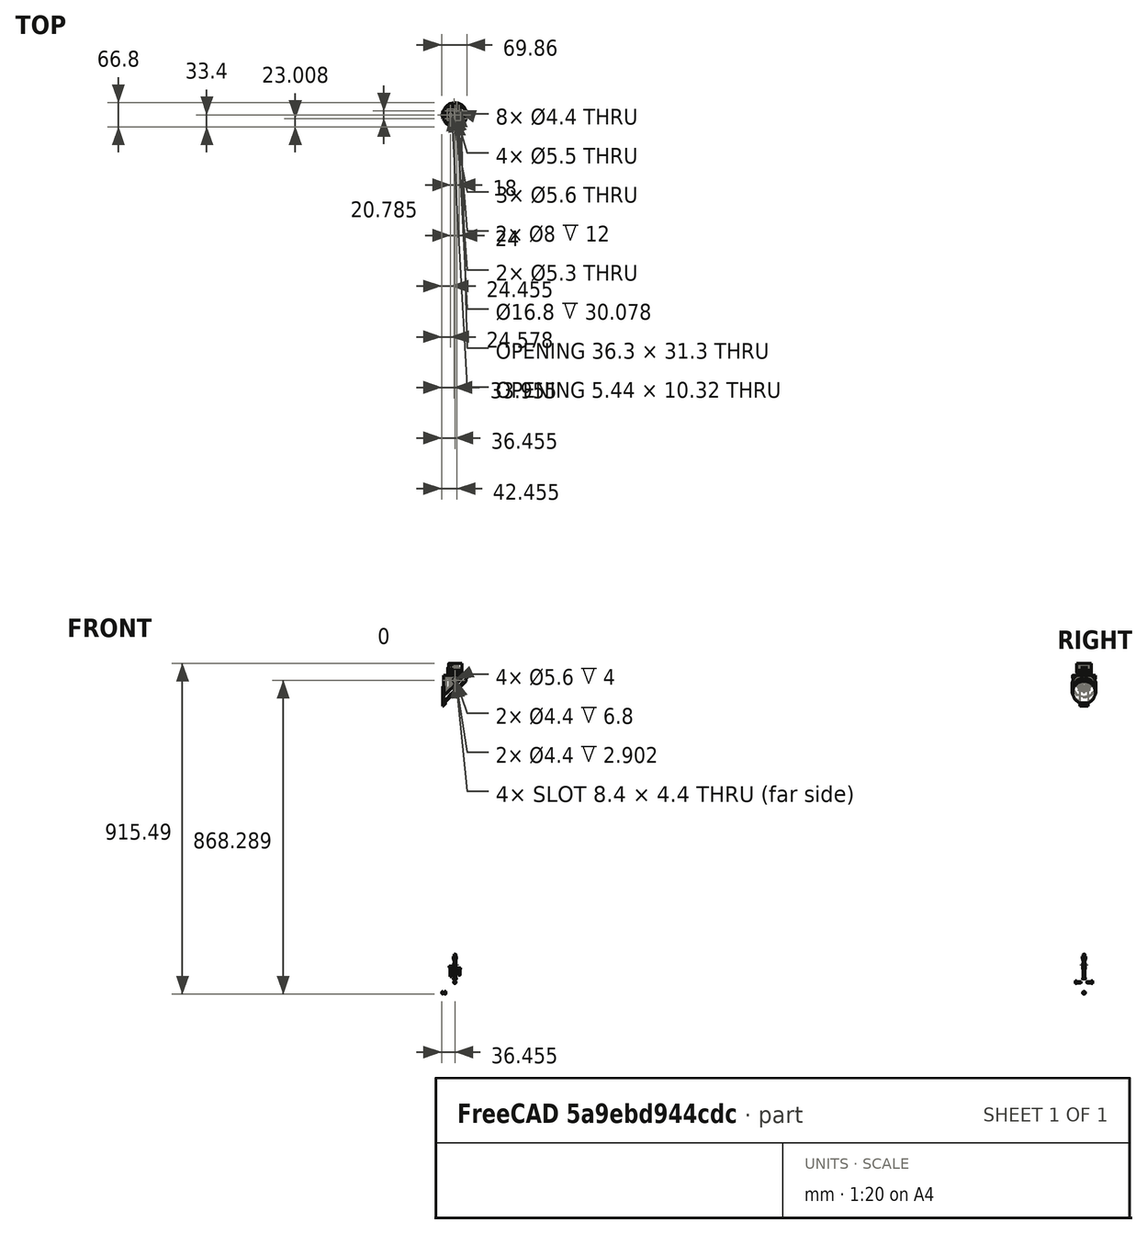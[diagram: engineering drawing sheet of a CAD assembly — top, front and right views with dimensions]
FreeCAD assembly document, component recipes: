
FREECAD ASSEMBLY — COMPONENT RECIPES ("SecondaryMirrorCell")

This assembly document has 9 components, labeled P0..P8 below (a component is one placed body or linked part). 9 of them carry a construction recipe — the FreeCAD feature program that regenerates the part from scratch, quoted from this document or its linked companion documents; the rest are supplied as boundary geometry only. No exploded tour is included for this assembly.
NOTE — document 2 of 2 of this assembly tour. The two overview renders and the header above are repeated from document 1; the component sections below continue where the previous document stopped.
COMPONENT P7 — recipe-attached ("SpiderHub_PushPull", modeled in this document).
Construction recipe (the document's own serialized feature program — sketch geometry with constraints, then the solid features built on it; lengths are millimeters unless a unit is written):

FEATURE [PartDesign::Plane] DatumPlane040  label="SpiderHub_PushPull_DatumPlane_Top"
  AttachmentOffset = pos=(0,0,20) rot=(0,0,1;0rad)
  Length = 60
  MapMode = 5
  Placement = pos=(0,0,20) rot=(0,0,1;0rad)
  ResizeMode = 0
  Support = -> [XY_Plane105]
  Width = 60
  expr: .AttachmentOffset.Base.z = <<Common>>#<<Parameters>>.sec_stalkheight
FEATURE [PartDesign::CoordinateSystem] Local_CS242  label="LCS_SpiderHub_PushPull_Lower"
  AttacherType = Attacher::AttachEngine3D
  AttachmentOffset = pos=(0,0,0) rot=(0,0,1;1.5708rad)
  MapMode = 5
  Placement = pos=(0,0,0) rot=(0,0,1;1.5708rad)
  Support = -> [XY_Plane105]
FEATURE [PartDesign::CoordinateSystem] Local_CS241  label="LCS_SpiderHub_PushPull_BoltTilt"
  AttacherType = Attacher::AttachEngine3D
  AttachmentOffset = pos=(-12,0,8) rot=(0,0,1;0rad)
  MapMode = 5
  Placement = pos=(-12,0,8) rot=(0,0,1;0rad)
  Support = -> [XY_Plane105]
  expr: .AttachmentOffset.Base.x = -<<Common>>#<<Parameters>>.sec_cpointpos
  expr: .AttachmentOffset.Base.z = <<Common>>#<<Parameters>>.sec_pthick
FEATURE [PartDesign::CoordinateSystem] Local_CS240  label="LCS_SpiderHub_PushPull_BoltZrot"
  AttacherType = Attacher::AttachEngine3D
  AttachmentOffset = pos=(12,0,8) rot=(0,0,1;0rad)
  MapMode = 5
  Placement = pos=(12,0,8) rot=(0,0,1;0rad)
  Support = -> [XY_Plane105]
  expr: .AttachmentOffset.Base.x = <<Common>>#<<Parameters>>.sec_cpointpos
  expr: .AttachmentOffset.Base.z = <<Common>>#<<Parameters>>.sec_pthick
FEATURE [PartDesign::CoordinateSystem] Local_CS239  label="LCS_SpiderHub_PushPull_Upper"
  AttacherType = Attacher::AttachEngine3D
  AttachmentOffset = pos=(0,0,20) rot=(0,0,1;1.5708rad)
  MapMode = 5
  Placement = pos=(0,0,20) rot=(0,0,1;1.5708rad)
  Support = -> [XY_Plane105]
  expr: .AttachmentOffset.Base.z = <<Common>>#<<Parameters>>.sec_stalkheight
FEATURE [PartDesign::ShapeBinder] ShapeBinder007  label="SpiderHub_PushPull_ShapeBinder"
  Support = -> [Binder]
  TraceSupport = false
FEATURE [Sketcher::SketchObject] Sketch168  label="SpiderHub_PushPull_Main_Sketch"
  ExternalGeometry = -> [ShapeBinder007]
  FullyConstrained = true
  MapMode = 5
  Support = -> [XY_Plane105]
  expr: Constraints[0] = <<Common>>#<<Parameters>>.sec_centralbolt * 1.1
  expr: Constraints[20] = <<Common>>#<<Parameters>>.sec_fillet
  expr: Constraints[23] = <<Common>>#<<Parameters>>.sec_cpointpos
  expr: Constraints[36] = <<Common>>#<<Parameters>>.sec_collbolt * 1.1
  sketch-geometry (16):
    g0: Circle CenterX=0 CenterY=0 CenterZ=0 NormalX=0 NormalY=0 NormalZ=1 AngleXU=0 Radius=2.75
    g1: LineSegment StartX=-19.1267 StartY=4.61831 StartZ=0 EndX=-4.61831 EndY=19.1267 EndZ=0
    g2: LineSegment StartX=-19.1267 StartY=-4.61831 StartZ=0 EndX=-4.61831 EndY=-19.1267 EndZ=0
    g3: ArcOfCircle CenterX=0 CenterY=0 CenterZ=0 NormalX=0 NormalY=0 NormalZ=1 AngleXU=0 Radius=20 StartAngle=4.53343 EndAngle=8.03294
    g4: ArcOfCircle CenterX=-3.2041 CenterY=17.7125 CenterZ=0 NormalX=0 NormalY=0 NormalZ=1 AngleXU=0 Radius=2 StartAngle=1.74976 EndAngle=2.35619
    g5: ArcOfCircle CenterX=-3.2041 CenterY=-17.7125 CenterZ=0 NormalX=0 NormalY=0 NormalZ=1 AngleXU=0 Radius=2 StartAngle=3.92699 EndAngle=4.53343
    g6: ArcOfCircle CenterX=0 CenterY=0 CenterZ=0 NormalX=0 NormalY=0 NormalZ=1 AngleXU=0 Radius=20 StartAngle=2.96263 EndAngle=3.32055
    g7: ArcOfCircle CenterX=-17.7125 CenterY=-3.2041 CenterZ=0 NormalX=0 NormalY=0 NormalZ=1 AngleXU=0 Radius=2 StartAngle=3.32055 EndAngle=3.92699
    g8: ArcOfCircle CenterX=-17.7125 CenterY=3.2041 CenterZ=0 NormalX=0 NormalY=0 NormalZ=1 AngleXU=0 Radius=2 StartAngle=2.35619 EndAngle=2.96263
    g9: Circle CenterX=0 CenterY=0 CenterZ=0 NormalX=0 NormalY=0 NormalZ=1 AngleXU=0 Radius=12
    g10: LineSegment StartX=-12 StartY=0 StartZ=0 EndX=6 EndY=-10.3923 EndZ=0
    g11: LineSegment StartX=6 StartY=-10.3923 StartZ=0 EndX=6 EndY=10.3923 EndZ=0
    g12: LineSegment StartX=6 StartY=10.3923 StartZ=0 EndX=-12 EndY=0 EndZ=0
    g13: Circle CenterX=-12 CenterY=0 CenterZ=0 NormalX=0 NormalY=0 NormalZ=1 AngleXU=0 Radius=2.2
    g14: Circle CenterX=6 CenterY=10.3923 CenterZ=0 NormalX=0 NormalY=0 NormalZ=1 AngleXU=0 Radius=2.2
    g15: Circle CenterX=6 CenterY=-10.3923 CenterZ=0 NormalX=0 NormalY=0 NormalZ=1 AngleXU=0 Radius=2.2
  constraints (39):
    c: Diameter(g0) = 5.5
    c: Equal(g1,g2)
    c: PointOnObject(g1,g-5)
    c: PointOnObject(g2,g-4)
    c: Coincident(g3,g0)
    c: Coincident(g0,g-3)
    c: Equal(g3,g-3)
    c: Tangent(g1,g4) = 1.5708
    c: Tangent(g2,g5) = -1.5708
    c: Tangent(g3,g5) = -1.5708
    c: Parallel(g2,g-4)
    c: Parallel(g1,g-5)
    c: Equal(g4,g5)
    c: Tangent(g3,g4) = -1.5708
    c: Coincident(g6,g0)
    c: PointOnObject(g6,g-3)
    c: Tangent(g8,g1) = 1.5708
    c: Tangent(g8,g6) = -1.5708
    c: Tangent(g7,g6) = -1.5708
    c: Tangent(g7,g2) = -1.5708
    c: Radius(g8) = 2
    c: Equal(g4,g8)
    c: Coincident(g9,g0)
    c: Radius(g9) = 12
    c: Coincident(g10,g11)
    c: Coincident(g11,g12)
    c: Coincident(g12,g10)
    c: Equal(g10,g11)
    c: Equal(g10,g12)
    c: PointOnObject(g12,g-1)
    c: PointOnObject(g10,g9)
    c: PointOnObject(g10,g9)
    c: PointOnObject(g11,g9)
    c: Coincident(g13,g10)
    c: Coincident(g14,g11)
    c: Coincident(g15,g10)
    c: Diameter(g15) = 4.4
    c: Equal(g15,g14)
    c: Equal(g15,g13)
FEATURE [Sketcher::SketchObject] Sketch169  label="SpiderHub_PushPull_CounterBore_Sketch"
  ExternalGeometry = -> [ShapeBinder007]
  FullyConstrained = true
  MapMode = 5
  Placement = pos=(0,0,20) rot=(0,0,1;0rad)
  Support = -> [DatumPlane040]
  expr: Constraints[0] = <<Common>>#<<Parameters>>.sec_cpointpos
  expr: Constraints[24] = <<Common>>#<<Parameters>>.sec_fillet
  expr: Constraints[3] = <<Common>>#<<Parameters>>.sec_collbolt
  sketch-geometry (18):
    g0: Circle CenterX=0 CenterY=0 CenterZ=0 NormalX=0 NormalY=0 NormalZ=1 AngleXU=0 Radius=12
    g1: ArcOfCircle CenterX=-12 CenterY=0 CenterZ=0 NormalX=0 NormalY=0 NormalZ=1 AngleXU=0 Radius=4 StartAngle=4.71239 EndAngle=7.85398
    g2: LineSegment StartX=-12 StartY=4 StartZ=0 EndX=-14.9166 EndY=4 EndZ=0
    g3: LineSegment StartX=-12 StartY=-4 StartZ=0 EndX=-14.9166 EndY=-4 EndZ=0
    g4: LineSegment StartX=-21 StartY=7.41423 StartZ=0 EndX=-21 EndY=-7.41423 EndZ=0
    g5: ArcOfCircle CenterX=-14.9166 CenterY=6 CenterZ=0 NormalX=0 NormalY=0 NormalZ=1 AngleXU=0 Radius=2 StartAngle=2.35619 EndAngle=4.71239
    g6: GeomPoint X=21 Y=0 Z=0
    g7: GeomPoint X=20 Y=0 Z=0
    g8: GeomPoint X=-20 Y=0 Z=0
    g9: GeomPoint X=-21 Y=0 Z=0
    g10: LineSegment StartX=-16.3308 StartY=7.41423 StartZ=0 EndX=-21 EndY=7.41423 EndZ=0
    g11: LineSegment StartX=-16.3308 StartY=-7.41423 StartZ=0 EndX=-21 EndY=-7.41423 EndZ=0
    g12: ArcOfCircle CenterX=-14.9166 CenterY=-6 CenterZ=0 NormalX=0 NormalY=0 NormalZ=1 AngleXU=0 Radius=2 StartAngle=1.5708 EndAngle=3.927
    g13: LineSegment StartX=-12 StartY=0 StartZ=0 EndX=6 EndY=10.3923 EndZ=0
    g14: LineSegment StartX=6 StartY=10.3923 StartZ=0 EndX=6 EndY=-10.3923 EndZ=0
    g15: LineSegment StartX=6 StartY=-10.3923 StartZ=0 EndX=-12 EndY=0 EndZ=0
    g16: Circle CenterX=6 CenterY=10.3923 CenterZ=0 NormalX=0 NormalY=0 NormalZ=1 AngleXU=0 Radius=4
    g17: Circle CenterX=6 CenterY=-10.3923 CenterZ=0 NormalX=0 NormalY=0 NormalZ=1 AngleXU=0 Radius=4
  constraints (46):
    c: Radius(g0) = 12
    c: Coincident(g0,g-1)
    c: PointOnObject(g1,g0)
    c: Radius(g1) = 4
    c: Horizontal(g2)
    c: Horizontal(g3)
    c: Vertical(g4)
    c: PointOnObject(g7,g-3)
    c: PointOnObject(g8,g-3)
    c: PointOnObject(g9,g4)
    c: PointOnObject(g9,g-1)
    c: PointOnObject(g8,g-1)
    c: DistanceX(g9,g8) = 1
    c: PointOnObject(g7,g-1)
    c: PointOnObject(g6,g-1)
    c: DistanceX(g7,g6) = 1
    c: PointOnObject(g11,g-5)
    c: PointOnObject(g5,g-4)
    c: Coincident(g10,g5)
    c: Coincident(g10,g4)
    c: Coincident(g11,g4)
    c: Horizontal(g11)
    c: Horizontal(g10)
    c: Tangent(g5,g-4)
    c: Radius(g5) = 2
    c: Tangent(g5,g2) = 1.5708
    c: Coincident(g12,g11)
    c: Tangent(g12,g-5)
    c: Tangent(g12,g3) = -1.5708
    c: Equal(g12,g5)
    c: PointOnObject(g13,g-1)
    c: PointOnObject(g13,g0)
    c: Coincident(g14,g13)
    c: PointOnObject(g14,g0)
    c: Coincident(g15,g14)
    c: Coincident(g15,g13)
    c: Equal(g13,g14)
    c: Equal(g14,g15)
    c: Coincident(g1,g3)
    c: Coincident(g1,g13)
    c: Equal(g2,g3)
    c: Coincident(g16,g13)
    c: Coincident(g17,g14)
    c: Equal(g17,g16)
    c: Equal(g16,g1)
    c: Tangent(g2,g1) = -1.5708
FEATURE [PartDesign::Plane] DatumPlane041  label="SpiderHub_PushPull_DatumPlane_SpiderHole"
  Length = 82.6027
  MapMode = 14
  Placement = pos=(-11.8725,-11.8725,0) rot=(0.862856,-0.357407,-0.357407;1.71777rad)
  ResizeMode = 0
  Support = -> [ShapeBinder007,Z_Axis087]
  Width = 61.8921
FEATURE [Sketcher::SketchObject] Sketch170  label="SpiderHub_PushPull_SpiderHole_Sketch"
  ExternalGeometry = -> [ShapeBinder007]
  FullyConstrained = true
  MapMode = 5
  Placement = pos=(-11.8725,-11.8725,0) rot=(0.862856,-0.357407,-0.357407;1.71777rad)
  Support = -> [DatumPlane041]
  expr: Constraints[0] = <<Common>>#<<Parameters>>.sec_collbolt
  expr: Constraints[3] = <<Common>>#<<Parameters>>.sec_stalkheight / 4
  expr: Constraints[4] = <<Common>>#<<Parameters>>.sec_stalkheight / 4
  expr: Constraints[5] = <<Common>>#<<Parameters>>.sec_stalkheight / 2
  expr: Constraints[6] = <<Common>>#<<Parameters>>.sec_collbolt * 1.5
  expr: Constraints[8] = <<Common>>#<<Parameters>>.sec_sidebolt * 1.25
  sketch-geometry (3):
    g0: Circle CenterX=5.86674 CenterY=5 CenterZ=0 NormalX=0 NormalY=0 NormalZ=1 AngleXU=0 Radius=2
    g1: Circle CenterX=5.86674 CenterY=15 CenterZ=0 NormalX=0 NormalY=0 NormalZ=1 AngleXU=0 Radius=2
    g2: LineSegment StartX=5.86674 StartY=15 StartZ=0 EndX=5.86674 EndY=0 EndZ=0
  constraints (9):
    c: Diameter(g0) = 4
    c: Equal(g0,g1)
    c: Vertical(g2)
    c: PointOnObject(g0,g2) = 5
    c: DistanceY(g2,g0) = 5
    c: DistanceY(g0,g1) = 10
    c: PointOnObject(g2,g-1) = 6
    c: Coincident(g2,g1)
    c: DistanceX(g2,g-3) = 5
FEATURE [PartDesign::Plane] DatumPlane042  label="SpiderHub_PushPull_DatumPlane_SpiderNut"
  AttachmentOffset = pos=(0,0,-3) rot=(0,0,1;0rad)
  Length = 82.6027
  MapMode = 5
  Placement = pos=(-9.75121,-9.75121,0) rot=(0.862856,-0.357407,-0.357407;1.71777rad)
  ResizeMode = 0
  Support = -> [DatumPlane041]
  Width = 61.8921
  expr: .AttachmentOffset.Base.z = -<<Common>>#<<Parameters>>.sec_fthick
FEATURE [Sketcher::SketchObject] Sketch171  label="SpiderHub_PushPull_SpiderNut_Sketch"
  ExternalGeometry = -> [Sketch170]
  FullyConstrained = true
  MapMode = 5
  Placement = pos=(-9.75121,-9.75121,0) rot=(0.862856,-0.357407,-0.357407;1.71777rad)
  Support = -> [DatumPlane042]
  sketch-geometry (14):
    g0: LineSegment StartX=9.51674 StartY=12.8927 StartZ=0 EndX=9.51674 EndY=26 EndZ=0
    g1: LineSegment StartX=2.21674 StartY=26 StartZ=0 EndX=2.21674 EndY=12.8927 EndZ=0
    g2: LineSegment StartX=2.21674 StartY=12.8927 StartZ=0 EndX=5.86674 EndY=10.7853 EndZ=0
    g3: LineSegment StartX=5.86674 StartY=10.7853 StartZ=0 EndX=9.51674 EndY=12.8927 EndZ=0
    g4: Circle CenterX=5.86674 CenterY=15 CenterZ=0 NormalX=0 NormalY=0 NormalZ=1 AngleXU=0 Radius=4.21466
    g5: LineSegment StartX=9.51674 StartY=-6 StartZ=0 EndX=9.51674 EndY=7.10733 EndZ=0
    g6: LineSegment StartX=9.51674 StartY=7.10733 StartZ=0 EndX=5.86674 EndY=9.21466 EndZ=0
    g7: LineSegment StartX=5.86674 StartY=9.21466 StartZ=0 EndX=2.21674 EndY=7.10733 EndZ=0
    g8: LineSegment StartX=2.21674 StartY=7.10733 StartZ=0 EndX=2.21674 EndY=-6 EndZ=0
    g9: Circle CenterX=5.86674 CenterY=5 CenterZ=0 NormalX=0 NormalY=0 NormalZ=1 AngleXU=0 Radius=4.21466
    g10: LineSegment StartX=5.86674 StartY=15 StartZ=0 EndX=5.86674 EndY=10.7853 EndZ=0
    g11: LineSegment StartX=5.86674 StartY=5 StartZ=0 EndX=5.86674 EndY=9.21466 EndZ=0
    g12: LineSegment StartX=2.21674 StartY=-6 StartZ=0 EndX=9.51674 EndY=-6 EndZ=0
    g13: LineSegment StartX=2.21674 StartY=26 StartZ=0 EndX=9.51674 EndY=26 EndZ=0
  constraints (38):
    c: Coincident(g1,g2)
    c: Coincident(g2,g3)
    c: Coincident(g3,g0)
    c: PointOnObject(g1,g4)
    c: PointOnObject(g2,g4)
    c: PointOnObject(g3,g4)
    c: Coincident(g4,g-3)
    c: Coincident(g5,g6)
    c: Coincident(g6,g7)
    c: Coincident(g7,g8)
    c: PointOnObject(g5,g9)
    c: PointOnObject(g6,g9)
    c: PointOnObject(g7,g9)
    c: Coincident(g9,g-4)
    c: Equal(g4,g9)
    c: Vertical(g1)
    c: Vertical(g8)
    c: Vertical(g0)
    c: Coincident(g10,g4)
    c: Coincident(g10,g2)
    c: Coincident(g11,g9)
    c: Coincident(g11,g6)
    c: Vertical(g10)
    c: Angle(g3,g2) = 2.0944
    c: DistanceX(g1,g0) = 7.3
    c: Equal(g3,g2)
    c: Equal(g7,g6)
    c: Equal(g6,g3)
    c: Vertical(g11)
    c: Vertical(g5)
    c: Coincident(g12,g8)
    c: Coincident(g12,g5)
    c: Coincident(g13,g1)
    c: Coincident(g13,g0)
    c: Horizontal(g13)
    c: Equal(g0,g5)
    c: Horizontal(g12)
    c: DistanceY(g8) = -6
FEATURE [Sketcher::SketchObject] Sketch174  label="SpiderHub_PushPull_LowerPlate_Sketch"
  ExternalGeometry = -> [ShapeBinder007]
  FullyConstrained = true
  MapMode = 5
  Support = -> [XY_Plane105]
  expr: Constraints[15] = <<Common>>#<<Parameters>>.sec_collbolt * 1.1
  expr: Constraints[19] = <<Common>>#<<Parameters>>.sec_centralbolt * 1.1
  sketch-geometry (9):
    g0: Circle CenterX=0 CenterY=0 CenterZ=0 NormalX=0 NormalY=0 NormalZ=1 AngleXU=0 Radius=20
    g1: LineSegment StartX=-12 StartY=0 StartZ=0 EndX=6 EndY=-10.3923 EndZ=0
    g2: LineSegment StartX=6 StartY=-10.3923 StartZ=0 EndX=6 EndY=10.3923 EndZ=0
    g3: LineSegment StartX=6 StartY=10.3923 StartZ=0 EndX=-12 EndY=0 EndZ=0
    g4: Circle CenterX=0 CenterY=0 CenterZ=0 NormalX=0 NormalY=0 NormalZ=1 AngleXU=0 Radius=12
    g5: Circle CenterX=6 CenterY=10.3923 CenterZ=0 NormalX=0 NormalY=0 NormalZ=1 AngleXU=0 Radius=2.2
    g6: Circle CenterX=6 CenterY=-10.3923 CenterZ=0 NormalX=0 NormalY=0 NormalZ=1 AngleXU=0 Radius=2.2
    g7: Circle CenterX=-12 CenterY=0 CenterZ=0 NormalX=0 NormalY=0 NormalZ=1 AngleXU=0 Radius=2.2
    g8: Circle CenterX=0 CenterY=0 CenterZ=0 NormalX=0 NormalY=0 NormalZ=1 AngleXU=0 Radius=2.75
  constraints (20):
    c: Coincident(g0,g-1)
    c: Coincident(g1,g2)
    c: Coincident(g2,g3)
    c: Coincident(g3,g1)
    c: Equal(g1,g2)
    c: Equal(g1,g3)
    c: PointOnObject(g1,g4)
    c: PointOnObject(g2,g4)
    c: PointOnObject(g3,g4)
    c: Coincident(g4,g0)
    c: Coincident(g3,g-4)
    c: Equal(g0,g-3)
    c: Coincident(g5,g2)
    c: Coincident(g6,g1)
    c: Coincident(g7,g1)
    c: Diameter(g7) = 4.4
    c: Equal(g7,g5)
    c: Equal(g7,g6)
    c: Coincident(g8,g0)
    c: Diameter(g8) = 5.5
FEATURE [PartDesign::Pad] Pad043  label="SpiderHub_PushPull_Main"
  Direction = (0,0,1)
  Length = 20
  Length2 = 100
  Profile = -> Sketch168
  Type = 0
  expr: Length = <<Common>>#<<Parameters>>.sec_stalkheight
FEATURE [PartDesign::Pad] Pad044  label="SpiderHub_PushPull_LowerPlate"
  BaseFeature = -> Pad043
  Direction = (0,0,1)
  Length = 5
  Length2 = 100
  Profile = -> Sketch174
  Reversed = true
  Type = 0
  expr: Length = <<Common>>#<<Parameters>>.sec_pthick - 3
FEATURE [PartDesign::Pocket] Pocket106  label="SpiderHub_PushPull_CounterBore"
  BaseFeature = -> Pad044
  Direction = (0,0,-1)
  Length = 12
  Length2 = 100
  Profile = -> Sketch169
  Type = 0
  expr: Length = <<Common>>#<<Parameters>>.sec_stalkheight - <<Common>>#<<Parameters>>.sec_pthick
FEATURE [Sketcher::SketchObject] Sketch175  label="SpiderHub_PushPull_LowerNut_Sketch"
  ExternalGeometry = -> [Pocket106]
  FullyConstrained = true
  MapMode = 5
  Placement = pos=(0,0,-5) rot=(1,0,0;3.14159rad)
  Support = -> [Pocket106]
  expr: Constraints[5] = <<Common>>#<<Parameters>>.acc_M4Bore
  sketch-geometry (3):
    g0: Circle CenterX=-12 CenterY=0 CenterZ=0 NormalX=0 NormalY=0 NormalZ=1 AngleXU=0 Radius=2.8
    g1: Circle CenterX=6 CenterY=10.3923 CenterZ=0 NormalX=0 NormalY=0 NormalZ=1 AngleXU=0 Radius=2.8
    g2: Circle CenterX=6 CenterY=-10.3923 CenterZ=0 NormalX=0 NormalY=0 NormalZ=1 AngleXU=0 Radius=2.8
  constraints (6):
    c: Coincident(g1,g-3)
    c: Coincident(g2,g-4)
    c: Equal(g0,g2)
    c: Equal(g2,g1)
    c: Coincident(g0,g-5)
    c: Diameter(g0) = 5.6
FEATURE [Sketcher::SketchObject] Sketch176  label="SpiderHub_PushPull_NutSupport_Sketch"
  FullyConstrained = false
  MapMode = 5
  Placement = pos=(0,0,-5) rot=(1,0,0;3.14159rad)
  Support = -> [Pad044]
  sketch-geometry (30):
    g0: LineSegment StartX=-13.7321 StartY=2.2 StartZ=0 EndX=-10.2679 EndY=2.2 EndZ=0
    g1: LineSegment StartX=-14.2 StartY=1.73205 StartZ=0 EndX=-14.2 EndY=-1.73205 EndZ=0
    g2: LineSegment StartX=-9.8 StartY=1.73205 StartZ=0 EndX=-9.8 EndY=-1.73205 EndZ=0
    g3: LineSegment StartX=-13.7321 StartY=-2.2 StartZ=0 EndX=-10.2679 EndY=-2.2 EndZ=0
    g4: ArcOfCircle CenterX=-12 CenterY=0 CenterZ=0 NormalX=0 NormalY=0 NormalZ=1 AngleXU=0 Radius=2.8 StartAngle=2.23774 EndAngle=2.47465
    g5: ArcOfCircle CenterX=-12 CenterY=0 CenterZ=0 NormalX=0 NormalY=0 NormalZ=1 AngleXU=0 Radius=2.8 StartAngle=0.666946 EndAngle=0.90385
    g6: ArcOfCircle CenterX=-12 CenterY=0 CenterZ=0 NormalX=0 NormalY=0 NormalZ=1 AngleXU=0 Radius=2.8 StartAngle=5.37934 EndAngle=5.61624
    g7: ArcOfCircle CenterX=-12 CenterY=0 CenterZ=0 NormalX=0 NormalY=0 NormalZ=1 AngleXU=0 Radius=2.8 StartAngle=3.80854 EndAngle=4.04544
    g8: LineSegment StartX=-12 StartY=2.2 StartZ=0 EndX=-12 EndY=-2.2 EndZ=0
    g9: LineSegment StartX=-14.2 StartY=0 StartZ=0 EndX=-9.8 EndY=0 EndZ=0
    g10: LineSegment StartX=4.26795 StartY=12.5923 StartZ=0 EndX=7.73205 EndY=12.5923 EndZ=0
    g11: LineSegment StartX=8.2 StartY=12.1244 StartZ=0 EndX=8.2 EndY=8.66025 EndZ=0
    g12: LineSegment StartX=7.73205 StartY=8.1923 StartZ=0 EndX=4.26795 EndY=8.1923 EndZ=0
    g13: LineSegment StartX=3.8 StartY=8.66025 StartZ=0 EndX=3.8 EndY=12.1244 EndZ=0
    g14: ArcOfCircle CenterX=6 CenterY=10.3923 CenterZ=0 NormalX=0 NormalY=0 NormalZ=1 AngleXU=0 Radius=2.8 StartAngle=2.23774 EndAngle=2.47465
    g15: ArcOfCircle CenterX=6 CenterY=10.3923 CenterZ=0 NormalX=0 NormalY=0 NormalZ=1 AngleXU=0 Radius=2.8 StartAngle=0.666946 EndAngle=0.90385
    g16: ArcOfCircle CenterX=6 CenterY=10.3923 CenterZ=0 NormalX=0 NormalY=0 NormalZ=1 AngleXU=0 Radius=2.8 StartAngle=5.37934 EndAngle=5.61624
    g17: ArcOfCircle CenterX=6 CenterY=10.3923 CenterZ=0 NormalX=0 NormalY=0 NormalZ=1 AngleXU=0 Radius=2.8 StartAngle=3.80854 EndAngle=4.04544
    g18: LineSegment StartX=3.8 StartY=10.3923 StartZ=0 EndX=8.2 EndY=10.3923 EndZ=0
    g19: LineSegment StartX=6 StartY=12.5923 StartZ=0 EndX=6 EndY=8.1923 EndZ=0
    g20: LineSegment StartX=3.8 StartY=-10.3923 StartZ=0 EndX=8.2 EndY=-10.3923 EndZ=0
    g21: LineSegment StartX=6 StartY=-8.1923 StartZ=0 EndX=6 EndY=-12.5923 EndZ=0
    g22: LineSegment StartX=4.26795 StartY=-8.1923 StartZ=0 EndX=7.73205 EndY=-8.1923 EndZ=0
    g23: LineSegment StartX=8.2 StartY=-8.66025 StartZ=0 EndX=8.2 EndY=-12.1244 EndZ=0
    g24: LineSegment StartX=7.73205 StartY=-12.5923 StartZ=0 EndX=4.26795 EndY=-12.5923 EndZ=0
    g25: LineSegment StartX=3.8 StartY=-12.1244 StartZ=0 EndX=3.8 EndY=-8.66025 EndZ=0
    g26: ArcOfCircle CenterX=6 CenterY=-10.3923 CenterZ=0 NormalX=0 NormalY=0 NormalZ=1 AngleXU=0 Radius=2.8 StartAngle=2.23774 EndAngle=2.47465
    g27: ArcOfCircle CenterX=6 CenterY=-10.3923 CenterZ=0 NormalX=0 NormalY=0 NormalZ=1 AngleXU=0 Radius=2.8 StartAngle=0.666946 EndAngle=0.90385
    g28: ArcOfCircle CenterX=6 CenterY=-10.3923 CenterZ=0 NormalX=0 NormalY=0 NormalZ=1 AngleXU=0 Radius=2.8 StartAngle=5.37934 EndAngle=5.61624
    g29: ArcOfCircle CenterX=6 CenterY=-10.3923 CenterZ=0 NormalX=0 NormalY=0 NormalZ=1 AngleXU=0 Radius=2.8 StartAngle=3.80854 EndAngle=4.04544
  constraints (67):
    c: Horizontal(g0)
    c: Vertical(g1)
    c: Vertical(g2)
    c: Horizontal(g3)
    c: Coincident(g4,g1)
    c: Coincident(g4,g0)
    c: Coincident(g5,g4)
    c: Coincident(g5,g0)
    c: Coincident(g6,g4)
    c: Coincident(g6,g2)
    c: Coincident(g7,g4)
    c: Coincident(g7,g3)
    c: Coincident(g5,g2)
    c: Coincident(g3,g6)
    c: Coincident(g1,g7)
    c: PointOnObject(g8,g0)
    c: PointOnObject(g8,g3)
    c: PointOnObject(g9,g1)
    c: PointOnObject(g9,g2)
    c: PointOnObject(g4,g9)
    c: PointOnObject(g4,g8)
    c: Horizontal(g9)
    c: Vertical(g8)
    c: Horizontal(g10)
    c: Horizontal(g12)
    c: Vertical(g11)
    c: Vertical(g13)
    c: Coincident(g14,g13)
    c: Coincident(g14,g10)
    c: Coincident(g15,g14)
    c: Coincident(g15,g10)
    c: Coincident(g15,g11)
    c: Coincident(g16,g14)
    c: Coincident(g16,g11)
    c: Coincident(g16,g12)
    c: Coincident(g17,g14)
    c: Coincident(g17,g12)
    c: Coincident(g17,g13)
    c: PointOnObject(g18,g13)
    c: PointOnObject(g18,g11)
    c: Horizontal(g18)
    c: PointOnObject(g19,g10)
    c: PointOnObject(g19,g12)
    c: Vertical(g19)
    c: PointOnObject(g14,g18)
    c: PointOnObject(g14,g19)
    c: Horizontal(g20)
    c: Vertical(g21)
    c: Horizontal(g22)
    c: Horizontal(g24)
    c: Vertical(g23)
    c: Vertical(g25)
    c: PointOnObject(g21,g22)
    c: PointOnObject(g21,g24)
    c: PointOnObject(g20,g23)
    c: PointOnObject(g20,g25)
    c: Coincident(g26,g25)
    c: Coincident(g26,g22)
    c: Coincident(g27,g26)
    c: Coincident(g27,g22)
    c: Coincident(g27,g23)
    c: Coincident(g28,g26)
    c: Coincident(g28,g23)
    c: Coincident(g28,g24)
    c: Coincident(g29,g26)
    c: Coincident(g29,g24)
    c: Coincident(g29,g25)
FEATURE [PartDesign::Hole] Hole053  label="SpiderHub_PushPull_SpiderHole"
  BaseFeature = -> Pocket106
  CustomThreadClearance = 0
  Depth = 8
  DepthType = 0
  Diameter = 3.3
  DrillForDepth = false
  DrillPoint = 1
  DrillPointAngle = 118
  HoleCutCountersinkAngle = 90
  HoleCutCustomValues = false
  HoleCutDepth = 0
  HoleCutDiameter = 6.1
  HoleCutType = 0
  ModelThread = false
  Profile = -> Sketch170
  Tapered = false
  TaperedAngle = 90
  ThreadClass = 0
  ThreadDepth = 8
  ThreadDepthType = 0
  ThreadDirection = 0
  ThreadFit = 0
  ThreadSize = 11
  ThreadType = 1
  Threaded = true
  UseCustomThreadClearance = false
FEATURE [PartDesign::Mirrored] Mirrored011  label="SpiderHub_PushPull_Mirrored"
  BaseFeature = -> Hole053
  MirrorPlane = -> XZ_Plane087
  Originals = -> [Hole053]
FEATURE [PartDesign::CoordinateSystem] Local_CS243  label="LCS_SpiderHub_PushPull_FZ"
  AttacherType = Attacher::AttachEngine3D
  MapMode = 11
  Placement = pos=(-7.72411,-16.0209,15) rot=(0.281085,0.678598,-0.678598;3.68962rad)
  Support = -> [Mirrored011]
FEATURE [PartDesign::CoordinateSystem] Local_CS244  label="LCS_SpiderHub_PushPull_AZ"
  AttacherType = Attacher::AttachEngine3D
  MapMode = 11
  Placement = pos=(-7.72411,16.0209,15) rot=(-0.862856,-0.357407,0.357407;1.71777rad)
  Support = -> [Mirrored011]
FEATURE [PartDesign::Hole] Hole054  label="SpiderHub_PushPull_Insert"
  BaseFeature = -> Mirrored011
  CustomThreadClearance = 0
  Depth = 4
  DepthType = 0
  Diameter = 5.6
  DrillForDepth = false
  DrillPoint = 1
  DrillPointAngle = 80
  HoleCutCountersinkAngle = 90
  HoleCutCustomValues = false
  HoleCutDepth = 0
  HoleCutDiameter = 6.1
  HoleCutType = 0
  ModelThread = false
  Profile = -> Sketch175
  Tapered = false
  TaperedAngle = 90
  ThreadClass = 0
  ThreadDepth = 4
  ThreadDepthType = 0
  ThreadDirection = 0
  ThreadFit = 0
  ThreadSize = 0
  ThreadType = 0
  Threaded = false
  UseCustomThreadClearance = false
  expr: Diameter = <<Common>>#<<Parameters>>.acc_M4Bore
FEATURE [PartDesign::Body] Body022035  label="SpiderHub_PushPull"
  Group = -> [Sketch168,Sketch169,DatumPlane040,Local_CS242,Local_CS241,Local_CS240,Local_CS239,Sketch170,Local_CS243,Local_CS244,DatumPlane041,ShapeBinder007,DatumPlane042,Sketch171,Sketch174,Pad043,Pad044,Pocket106,Sketch175,Sketch176,Hole053,Mirrored011,Hole054]
  Origin = -> Origin087
  Placement = pos=(-3.125,0,896) rot=(0,0,1;0rad)
  Tip = -> Hole054
  expr: .Placement.Base.x = -<<Common>>#<<Parameters>>.sec_offset_x
  expr: .Placement.Base.z = <<Common>>#<<Parameters>>.datum_sec_upperhub
COMPONENT P8 — recipe-attached ("MirrorPad_Flat", modeled in this document).
Construction recipe (the document's own serialized feature program — sketch geometry with constraints, then the solid features built on it; lengths are millimeters unless a unit is written):

FEATURE [Sketcher::SketchObject] Sketch177  label="MirrorPad_Flat_Base_Sketch"
  FullyConstrained = true
  MapMode = 5
  Placement = pos=(0,0,0) rot=(1,0,0;1.5708rad)
  Support = -> [XZ_Plane088]
  expr: Constraints[10] = <<Common>>#<<Parameters>>.sec_padheight
  expr: Constraints[13] = <<Common>>#<<Parameters>>.sec_mtvar
  expr: Constraints[15] = <<Common>>#<<Parameters>>.sec_hubdia / 2
  expr: Constraints[17] = <<Common>>#<<Parameters>>.sec_hubdia * 0.75 / 2
  expr: Constraints[5] = <<Common>>#<<Parameters>>.sec_fillet
  sketch-geometry (6):
    g0: LineSegment StartX=-18 StartY=-14 StartZ=0 EndX=15 EndY=19 EndZ=0
    g1: LineSegment StartX=-20 StartY=30.0779 StartZ=0 EndX=-20 EndY=-14 EndZ=0
    g2: LineSegment StartX=-20 StartY=-14 StartZ=0 EndX=-18 EndY=-14 EndZ=0
    g3: LineSegment StartX=15 StartY=19 StartZ=0 EndX=15 EndY=30.0779 EndZ=0
    g4: LineSegment StartX=15 StartY=30.0779 StartZ=0 EndX=-20 EndY=30.0779 EndZ=0
    g5: GeomPoint X=0 Y=4 Z=0
  constraints (18):
    c: Angle(g-1,g0) = 0.785398
    c: Vertical(g1)
    c: Coincident(g2,g1)
    c: Coincident(g2,g0)
    c: Horizontal(g2)
    c: DistanceX(g2,g2) = 2
    c: Coincident(g3,g0)
    c: Vertical(g3)
    c: Coincident(g4,g3)
    c: Coincident(g1,g4)
    c: DistanceY(g1) = 30.0779
    c: PointOnObject(g5,g0)
    c: PointOnObject(g5,g-2)
    c: DistanceY(g-1,g5) = 4
    c: DistanceY(g3,g3) = 11.0779
    c: DistanceX(g1,g-1) = 20
    c: Horizontal(g4)
    c: DistanceX(g-1,g3) = 15
FEATURE [PartDesign::Pad] Pad045  label="MirrorPad_Flat_Base"
  Direction = (0,-1,-2e-16)
  Length = 30
  Length2 = 100
  Midplane = true
  Placement = pos=(0,0,0) rot=(1,0,0;1.5708rad)
  Profile = -> Sketch177
  Type = 0
  expr: Length = 2 * ceil(<<Common>>#<<Parameters>>.sec_cpointpos * cos(30)) + <<Common>>#<<Parameters>>.sec_tiltball
FEATURE [PartDesign::Plane] DatumPlane044  label="MirrorPad_Flat_DatumPlane_Top"
  AttachmentOffset = pos=(0,0,30.0779) rot=(0,0,1;0rad)
  Length = 60
  MapMode = 5
  Placement = pos=(0,0,30.0779) rot=(0,0,1;0rad)
  ResizeMode = 0
  Support = -> [XY_Plane087]
  Width = 60
  expr: .AttachmentOffset.Base.z = <<Common>>#<<Parameters>>.sec_padheight
FEATURE [Sketcher::SketchObject] Sketch181  label="MirrorPad_Flat_Outer_Sketch"
  FullyConstrained = true
  MapMode = 5
  Support = -> [XY_Plane087]
  expr: Constraints[2] = <<Common>>#<<Parameters>>.sec_hubdia
  expr: Constraints[3] = <<Common>>#<<Parameters>>.sec_mdia * 2
  sketch-geometry (2):
    g0: Circle CenterX=0 CenterY=0 CenterZ=0 NormalX=0 NormalY=0 NormalZ=1 AngleXU=0 Radius=20
    g1: Circle CenterX=0 CenterY=0 CenterZ=0 NormalX=0 NormalY=0 NormalZ=1 AngleXU=0 Radius=62.5
  constraints (4):
    c: Coincident(g0,g-1)
    c: Coincident(g1,g0)
    c: Diameter(g0) = 40
    c: Diameter(g1) = 125
FEATURE [PartDesign::CoordinateSystem] Local_CS246  label="LCS_MirrorPad_Flat_TiltPlateAttachment"
  AttacherType = Attacher::AttachEngine3D
  AttachmentOffset = pos=(0,0,33.201) rot=(0,0,1;0rad)
  MapMode = 5
  Placement = pos=(0,0,33.201) rot=(0,0,1;0rad)
  Support = -> [XY_Plane087]
  expr: .AttachmentOffset.Base.z = <<Common>>#<<Parameters>>.sec_padheight + <<Common>>#<<Parameters>>.sec_tiltspacing
FEATURE [PartDesign::CoordinateSystem] Local_CS247  label="LCS_MirrorPad_Flat_SecondaryPad"
  AttacherType = Attacher::AttachEngine3D
  MapMode = 5
  Support = -> [XY_Plane087]
FEATURE [PartDesign::Plane] DatumPlane045  label="MirrorPad_Flat_DatumPlane_Cavity"
  AttachmentOffset = pos=(0,0,-4) rot=(0,0,1;0rad)
  Length = 60
  MapMode = 2
  Placement = pos=(0,0,26.0779) rot=(0,0,1;0rad)
  ResizeMode = 0
  Support = -> [DatumPlane044]
  Width = 60
  expr: .AttachmentOffset.Base.z = -<<Common>>#<<Parameters>>.sec_pthick / 2
FEATURE [Sketcher::SketchObject] Sketch178  label="MirrorPad_Flat_Cavity_Sketch"
  FullyConstrained = true
  MapMode = 5
  Placement = pos=(0,0,26.0779) rot=(0,0,1;0rad)
  Support = -> [DatumPlane045]
  sketch-geometry (1):
    g0: Circle CenterX=0 CenterY=0 CenterZ=0 NormalX=0 NormalY=0 NormalZ=1 AngleXU=0 Radius=8.4
  constraints (2):
    c: Coincident(g0,g-1)
    c: Radius(g0) = 8.4
FEATURE [Sketcher::SketchObject] Sketch180  label="MirrorPad_Flat_CentralHole_Sketch"
  FullyConstrained = true
  MapMode = 5
  Placement = pos=(0,0,26.0779) rot=(0,0,1;0rad)
  Support = -> [DatumPlane045]
  expr: Constraints[1] = <<Common>>#<<Parameters>>.sec_centralbolt * 1.3
  sketch-geometry (1):
    g0: Circle CenterX=0 CenterY=0 CenterZ=0 NormalX=0 NormalY=0 NormalZ=1 AngleXU=0 Radius=3.25
  constraints (2):
    c: Coincident(g0,g-1)
    c: Diameter(g0) = 6.5
FEATURE [PartDesign::CoordinateSystem] Local_CS245  label="LCS_MirrorPad_Flat_HubPoint"
  AttacherType = Attacher::AttachEngine3D
  MapMode = 5
  Placement = pos=(0,0,26.0779) rot=(0,0,1;0rad)
  Support = -> [DatumPlane045]
  expr: .AttachmentOffset.Base.z = 0
FEATURE [PartDesign::Pocket] Pocket110  label="MirrorPad_Flat_Cavity"
  BaseFeature = -> Pad045
  Direction = (0,0,-1)
  Length = 5
  Length2 = 100
  Placement = pos=(0,0,0) rot=(1,0,0;1.5708rad)
  Profile = -> Sketch178
  Type = 1
FEATURE [PartDesign::Pocket] Pocket111  label="MirrorPad_Flat_CentralHole"
  BaseFeature = -> Pocket110
  Direction = (0,0,-1)
  Length = 5
  Length2 = 100
  Placement = pos=(0,0,0) rot=(1,0,0;1.5708rad)
  Profile = -> Sketch180
  Reversed = true
  Type = 1
FEATURE [PartDesign::Pocket] Pocket112  label="MirrorPad_Flat_Outer"
  BaseFeature = -> Pocket111
  Direction = (0,0,-1)
  Length = 5
  Length2 = 100
  Midplane = true
  Placement = pos=(0,0,0) rot=(1,0,0;1.5708rad)
  Profile = -> Sketch181
  Type = 1
FEATURE [Sketcher::SketchObject] Sketch183  label="MirrorPad_Flat_InnerShaft_Sketch"
  FullyConstrained = true
  MapMode = 5
  Placement = pos=(0,0,0) rot=(1,0,0;1.5708rad)
  Support = -> [XZ_Plane088]
  expr: Constraints[1] = <<Common>>#<<Parameters>>.sec_collbolt * 1.1
  expr: Constraints[2] = <<Common>>#<<Parameters>>.sec_mtvar + <<Common>>#<<Parameters>>.sec_hubdia / 4
  sketch-geometry (1):
    g0: Circle CenterX=0 CenterY=14 CenterZ=0 NormalX=0 NormalY=0 NormalZ=1 AngleXU=0 Radius=2.2
  constraints (3):
    c: PointOnObject(g0,g-2)
    c: Diameter(g0) = 4.4
    c: DistanceY(g0) = 14
FEATURE [Sketcher::SketchObject] Sketch182  label="MirrorPad_Flat_InnerNut_Sketch"
  ExternalGeometry = -> [Sketch183]
  FullyConstrained = true
  MapMode = 5
  Placement = pos=(0,0,0) rot=(1,0,0;1.5708rad)
  Support = -> [XZ_Plane088]
  sketch-geometry (10):
    g0: LineSegment StartX=2.10733 StartY=10.35 StartZ=0 EndX=4.21466 EndY=14 EndZ=0
    g1: LineSegment StartX=4.21466 StartY=14 StartZ=0 EndX=2.10733 EndY=17.65 EndZ=0
    g2: LineSegment StartX=2.10733 StartY=17.65 StartZ=0 EndX=-2.10733 EndY=17.65 EndZ=0
    g3: LineSegment StartX=-2.10733 StartY=17.65 StartZ=0 EndX=-4.21466 EndY=14 EndZ=0
    g4: LineSegment StartX=-4.21466 StartY=14 StartZ=0 EndX=-2.10733 EndY=10.35 EndZ=0
    g5: LineSegment StartX=-2.10733 StartY=10.35 StartZ=0 EndX=2.10733 EndY=10.35 EndZ=0
    g6: Circle CenterX=0 CenterY=14 CenterZ=0 NormalX=0 NormalY=0 NormalZ=1 AngleXU=0 Radius=4.21466
    g7: LineSegment StartX=-2.10733 StartY=17.65 StartZ=0 EndX=2.10733 EndY=10.35 EndZ=0
    g8: LineSegment StartX=2.10733 StartY=17.65 StartZ=0 EndX=-2.10733 EndY=10.35 EndZ=0
    g9: LineSegment StartX=4.21466 StartY=14 StartZ=0 EndX=-4.21466 EndY=14 EndZ=0
  constraints (26):
    c: Coincident(g0,g1)
    c: Coincident(g1,g2)
    c: Coincident(g2,g3)
    c: Coincident(g3,g4)
    c: Coincident(g4,g5)
    c: Coincident(g5,g0)
    c: PointOnObject(g0,g6)
    c: PointOnObject(g1,g6)
    c: PointOnObject(g2,g6)
    c: PointOnObject(g3,g6)
    c: PointOnObject(g4,g6)
    c: PointOnObject(g5,g6)
    c: Horizontal(g2)
    c: DistanceY(g0,g1) = 7.3
    c: Coincident(g7,g2)
    c: Coincident(g7,g0)
    c: Coincident(g8,g1)
    c: Coincident(g8,g4)
    c: Coincident(g9,g0)
    c: Coincident(g9,g3)
    c: Horizontal(g9)
    c: Angle(g9,g8) = 1.0472
    c: Angle(g7,g9) = 1.0472
    c: PointOnObject(g6,g8)
    c: PointOnObject(g6,g9)
    c: Coincident(g6,g-3)
FEATURE [PartDesign::Pocket] Pocket114  label="MirrorPad_Flat_InnerShaft"
  BaseFeature = -> Pocket112
  Direction = (0,1,2e-16)
  Length = 5
  Length2 = 100
  Midplane = true
  Placement = pos=(0,0,0) rot=(1,0,0;1.5708rad)
  Profile = -> Sketch183
  Type = 1
FEATURE [Sketcher::SketchObject] Sketch184  label="MirrorPad_Flat_InnerCut_Sketch"
  FullyConstrained = true
  MapMode = 5
  Placement = pos=(0,0,0) rot=(1,0,0;1.5708rad)
  Support = -> [XZ_Plane088]
  expr: Constraints[10] = -<<Common>>#<<Parameters>>.sec_mdia / 2
  expr: Constraints[11] = <<Common>>#<<Parameters>>.sec_hubdia / 8 + 1
  expr: Constraints[8] = -<<Common>>#<<Parameters>>.sec_hubdia * 0.75 / 2
  expr: Constraints[9] = <<Common>>#<<Parameters>>.sec_padheight - <<Common>>#<<Parameters>>.sec_pthick
  sketch-geometry (4):
    g0: LineSegment StartX=-21 StartY=22.0779 StartZ=0 EndX=-15 EndY=22.0779 EndZ=0
    g1: LineSegment StartX=-15 StartY=22.0779 StartZ=0 EndX=-15 EndY=-31.25 EndZ=0
    g2: LineSegment StartX=-15 StartY=-31.25 StartZ=0 EndX=-21 EndY=-31.25 EndZ=0
    g3: LineSegment StartX=-21 StartY=-31.25 StartZ=0 EndX=-21 EndY=22.0779 EndZ=0
  constraints (12):
    c: Coincident(g0,g1)
    c: Coincident(g1,g2)
    c: Coincident(g2,g3)
    c: Coincident(g3,g0)
    c: Horizontal(g0)
    c: Horizontal(g2)
    c: Vertical(g1)
    c: Vertical(g3)
    c: DistanceX(g0) = -15
    c: DistanceY(g0) = 22.0779
    c: DistanceY(g1) = -31.25
    c: DistanceX(g0,g0) = 6
FEATURE [PartDesign::CoordinateSystem] Local_CS250  label="LCS_MirrorPad_Flat_Top"
  AttacherType = Attacher::AttachEngine3D
  MapMode = 5
  Placement = pos=(0,0,30.0779) rot=(0,0,1;0rad)
  Support = -> [DatumPlane044]
FEATURE [PartDesign::Pocket] Pocket193  label="MirrorPad_Flat_InnerCut"
  BaseFeature = -> Pocket114
  Direction = (0,1,2e-16)
  Length = 5
  Length2 = 5
  Midplane = true
  Placement = pos=(0,0,0) rot=(1,0,0;1.5708rad)
  Profile = -> Sketch184
  ReferenceAxis = -> Sketch184 [N_Axis]
  Type = 1
FEATURE [Sketcher::SketchObject] Sketch286  label="MirrorPad_Flat_Insert_Sketch"
  ExternalGeometry = -> [Pocket114]
  FullyConstrained = true
  MapMode = 5
  Placement = pos=(0,-15,0) rot=(1,0,0;1.5708rad)
  Support = -> [Pad045]
  expr: Constraints[1] = <<Common>>#<<Parameters>>.acc_M4Bore
  sketch-geometry (1):
    g0: Circle CenterX=0 CenterY=14 CenterZ=0 NormalX=0 NormalY=0 NormalZ=1 AngleXU=0 Radius=2.8
  constraints (2):
    c: Coincident(g0,g-3)
    c: Diameter(g0) = 5.6
FEATURE [PartDesign::Pocket] Pocket194  label="MirrorPad_Flat_Insert"
  BaseFeature = -> Pocket193
  Direction = (0,1,-2e-16)
  Length = 4
  Length2 = 5
  Placement = pos=(0,0,0) rot=(1,0,0;1.5708rad)
  Profile = -> Sketch286
  ReferenceAxis = -> Sketch286 [N_Axis]
  Type = 0
FEATURE [PartDesign::Mirrored] Mirrored010  label="MirrorPad_Flat_Mirrored"
  BaseFeature = -> Pocket194
  MirrorPlane = -> XZ_Plane088
  Originals = -> [Pocket194]
  Placement = pos=(0,0,0) rot=(1,0,0;1.5708rad)
FEATURE [PartDesign::CoordinateSystem] Local_CS248  label="LCS_MirrorPad_Flat_SideNut_F"
  AttacherType = Attacher::AttachEngine3D
  MapMode = 11
  Placement = pos=(0,-15,14) rot=(0.57735,-0.57735,-0.57735;4.18879rad)
  Support = -> [Mirrored010]
FEATURE [PartDesign::CoordinateSystem] Local_CS249  label="LCS_MirrorPad_Flat_SideNut_A"
  AttacherType = Attacher::AttachEngine3D
  MapMode = 11
  Placement = pos=(0,15,14) rot=(0.57735,-0.57735,0.57735;2.0944rad)
  Support = -> [Mirrored010]
FEATURE [PartDesign::Chamfer] Chamfer004  label="MirrorPad_Flat_Chamfer"
  Angle = 45
  Base = -> Mirrored010 [Edge29,Edge24,Edge12,Edge15,Edge16,Edge19,Edge21,Edge3,Edge2,Edge1,Edge4,Edge5,Edge9,Edge8,Edge7,Edge6,Edge26,Edge30]
  BaseFeature = -> Mirrored010
  ChamferType = 0
  FlipDirection = false
  Placement = pos=(0,0,0) rot=(1,0,0;1.5708rad)
  Size = 0.4
  Size2 = 1
  SupportTransform = false
  UseAllEdges = false
FEATURE [PartDesign::Body] Body022036  label="MirrorPad_Flat"
  Group = -> [Sketch177,Pad045,Sketch178,Sketch180,DatumPlane044,Sketch181,Local_CS245,Local_CS246,Local_CS247,DatumPlane045,Pocket110,Pocket111,Pocket112,Sketch182,Sketch183,Pocket114,Sketch184,Local_CS248,Local_CS249,Local_CS250,Pocket193,Sketch286,Pocket194,Mirrored010,Chamfer004]
  Origin = -> Origin088
  Placement = pos=(-3.125,0,854.799) rot=(0,0,1;0rad)
  Tip = -> Chamfer004
  expr: .Placement.Base.x = -<<Common>>#<<Parameters>>.sec_offset_x
  expr: .Placement.Base.z = <<Common>>#<<Parameters>>.datum_sec_mirrorpad
PROVENANCE & LICENSES
A FreeCAD (.FCStd) document from a public repository crawl; recipes are the document's own serialized feature recipes (and, for linked parts, companion documents' recipes).
License: as declared in the source repository (recorded in the dataset sidecar).
